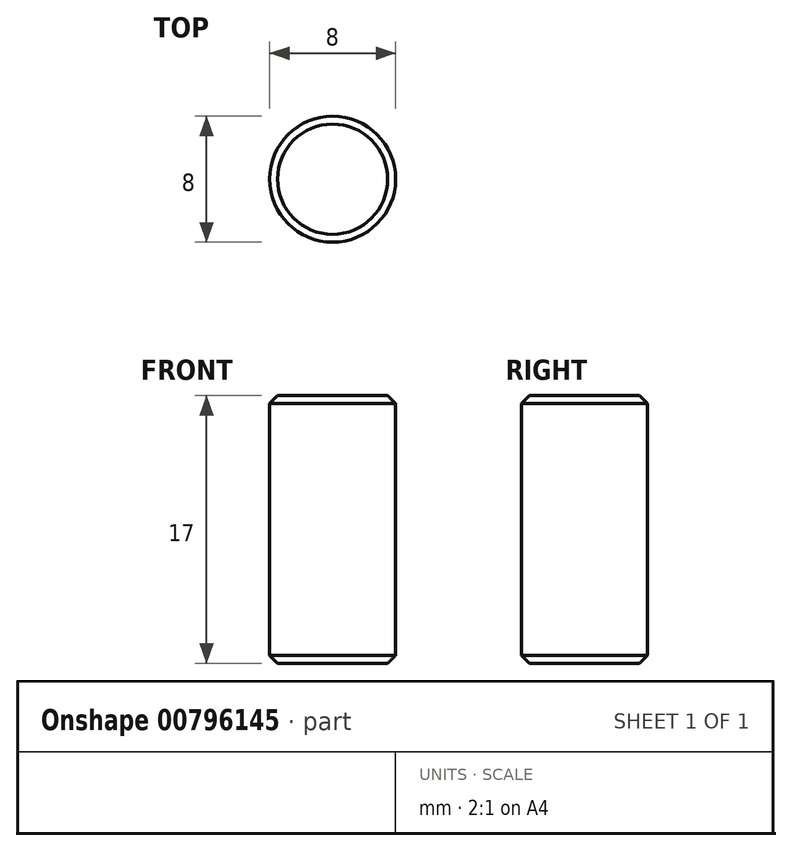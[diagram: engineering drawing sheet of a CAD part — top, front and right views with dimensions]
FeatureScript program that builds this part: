
annotation { "Feature Type Name" : "Feature", "Feature Type Description" : "" }
export const myFeature = defineFeature(function(context is Context, id is Id, definition is map)
    precondition{}
    {
        {
            var Q0;
            Q0=qCreatedBy(makeId("Top.planeOp"),FACE);
            var sketch = newSketch(context, id + "F0", { "sketchPlane" : qUnion([Q0])});
            skCircle(sketch, "E0", {"center": v(0, 0) * mm, "radius": 4 * mm});
            skSolve(sketch);
        }
        {
            var Q0;
            Q0=makeQuery(id+"F0.imprint","IMPRINT",FACE,{"disambiguationData":[TD([[makeQuery(id+"F0.imprint","IMPRINT",EDGE,{"derivedFrom":sQuery(id+"F0.wireOp",EDGE,"E0")}),1.0]])]});
            extrude(context, id + "F1", {"entities" : qUnion([Q0]), "endBound" : BoundingType.SYMMETRIC, "depth" : 17 * mm, "offsetDistance" : 25 * mm});
        }
        {
            var Q0;
            Q0=makeQuery(id+"F1.opExtrude","CAP_EDGE",EDGE,{"disambiguationData":[OSD([sQuery(id+"F0.wireOp",EDGE,"E0")])],"isStart":false});
            var Q1;
            Q1=makeQuery(id+"F1.opExtrude","CAP_EDGE",EDGE,{"disambiguationData":[OSD([sQuery(id+"F0.wireOp",EDGE,"E0")])],"isStart":true});
            chamfer(context, id + "F2", {"entities" : qUnion([Q0, Q1]), "width" : 0.5 * mm, "tangentPropagation" : true});
        }
    });
